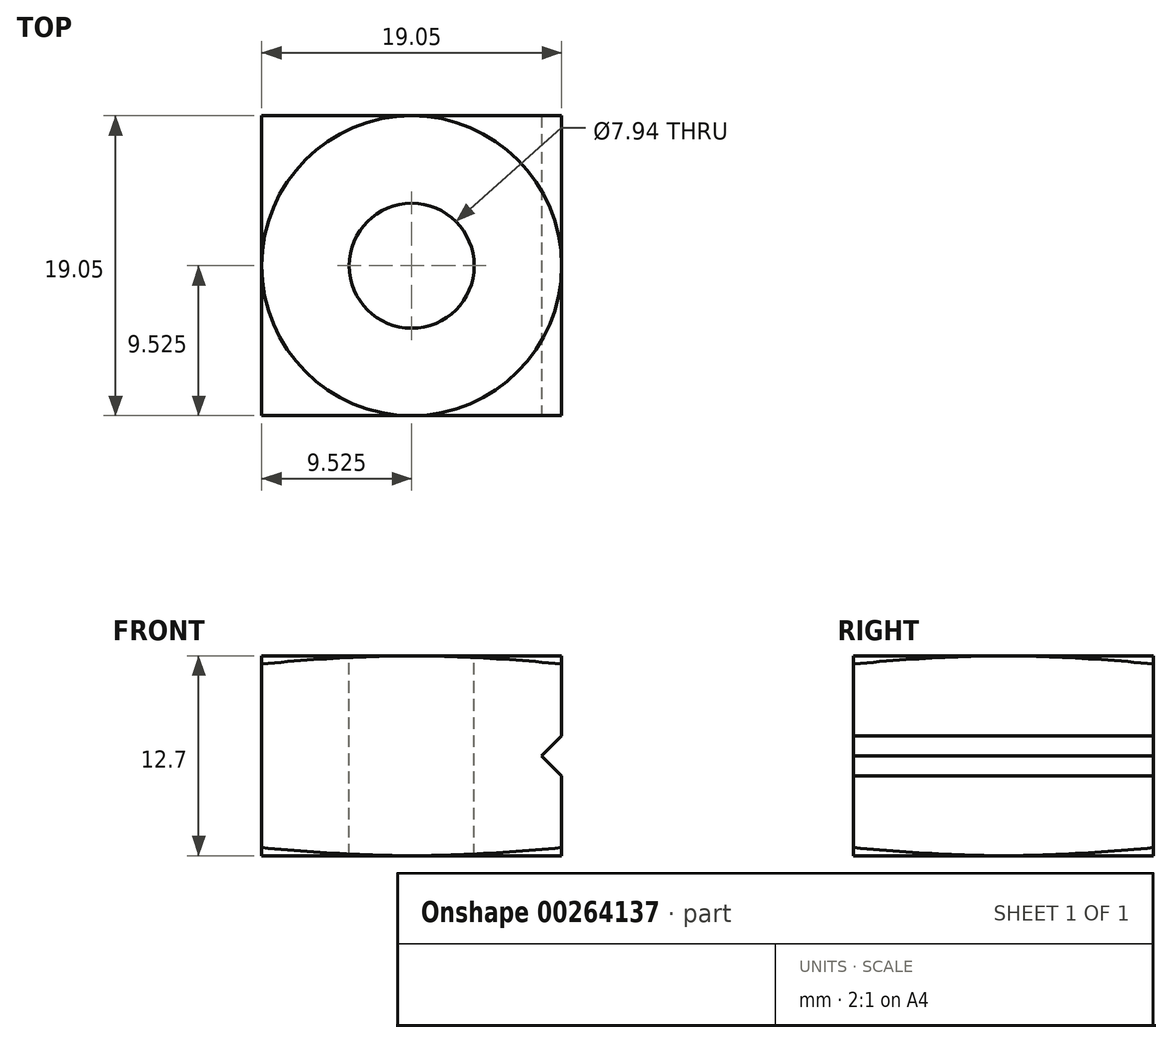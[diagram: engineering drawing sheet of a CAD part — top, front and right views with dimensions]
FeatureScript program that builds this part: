
annotation { "Feature Type Name" : "Feature", "Feature Type Description" : "" }
export const myFeature = defineFeature(function(context is Context, id is Id, definition is map)
    precondition{}
    {
        {
            var Q0;
            Q0=qCreatedBy(makeId("Top.planeOp"),FACE);
            var sketch = newSketch(context, id + "F0", { "sketchPlane" : qUnion([Q0])});
            skLineSegment(sketch, "E0.bottom", {"start": v(0, 0) * mm, "end": v(-19.05, 0) * mm});
            skLineSegment(sketch, "E0.top", {"start": v(0, 19.05) * mm, "end": v(-19.05, 19.05) * mm});
            skLineSegment(sketch, "E0.left", {"start": v(0, 0) * mm, "end": v(0, 19.05) * mm});
            skLineSegment(sketch, "E0.right", {"start": v(-19.05, 0) * mm, "end": v(-19.05, 19.05) * mm});
            skSolve(sketch);
        }
        {
            var Q0;
            Q0=makeQuery(id+"F0.imprint","IMPRINT",FACE,{"disambiguationData":[TD([[makeQuery(id+"F0.imprint","IMPRINT",EDGE,{"derivedFrom":sQuery(id+"F0.wireOp",EDGE,"E0.bottom")}),-1.0]])]});
            extrude(context, id + "F1", {"entities" : qUnion([Q0]), "depth" : 12.7 * mm});
        }
        {
            var Q0;
            Q0=makeQuery(id+"F1.opExtrude","CAP_FACE",FACE,{"disambiguationData":[OSD([sQuery(id+"F0.wireOp",EDGE,"E0.bottom"),sQuery(id+"F0.wireOp",EDGE,"E0.top"),sQuery(id+"F0.wireOp",EDGE,"E0.left"),sQuery(id+"F0.wireOp",EDGE,"E0.right")])],"isStart":false});
            var sketch = newSketch(context, id + "F2", { "sketchPlane" : qUnion([Q0])});
            skCircle(sketch, "E1", {"center": v(-9.53, 9.53) * mm, "radius": 3.97 * mm});
            skSolve(sketch);
        }
        {
            var Q0;
            Q0 = qSketchRegion(id + "F2", true);
            extrude(context, id + "F3", {"entities" : qUnion([Q0]), "operationType" : NewBodyOperationType.REMOVE, "endBound" : BoundingType.THROUGH_ALL, "oppositeDirection" : true, "depth" : 25.4 * mm});
        }
        {
            var Q0;
            Q0=makeQuery(id+"F2.imprint","IMPRINT",FACE,{"disambiguationData":[TD([[makeQuery(id+"F2.imprint","IMPRINT",EDGE,{"derivedFrom":sQuery(id+"F2.wireOp",EDGE,"E1")}),-1.0]])]});
            var sketch = newSketch(context, id + "F4", { "sketchPlane" : qUnion([Q0])});
            skCircle(sketch, "E2", {"center": v(-9.53, 9.53) * mm, "radius": 9.53 * mm});
            skSolve(sketch);
        }
        {
            var Q0;
            Q0=makeQuery(id+"F1.opExtrude","SWEPT_FACE",FACE,{"disambiguationData":[OSD([sQuery(id+"F0.wireOp",EDGE,"E0.bottom")])]});
            var Q1;
            Q1=makeQuery(id+"F1.opExtrude","SWEPT_FACE",FACE,{"disambiguationData":[OSD([sQuery(id+"F0.wireOp",EDGE,"E0.top")])]});
            cPlane(context, id + "F5", {"entities" : qUnion([Q0, Q1]), "cplaneType" : CPlaneType.MID_PLANE, "offset" : 25.4 * mm, "width" : 152.4 * mm, "height" : 152.4 * mm});
        }
        {
            var Q0;
            Q0=qCreatedBy(id+"F5.planeOp",FACE);
            var sketch = newSketch(context, id + "F6", { "sketchPlane" : qUnion([Q0])});
            skLineSegment(sketch, "E3.0.0", {"start": v(0, 0) * mm, "end": v(-19.05, 0) * mm});
            skLineSegment(sketch, "E3.0.1", {"start": v(-19.05, 0) * mm, "end": v(-19.05, 12.7) * mm});
            skLineSegment(sketch, "E3.0.2", {"start": v(-19.05, 12.7) * mm, "end": v(0, 12.7) * mm});
            skLineSegment(sketch, "E3.0.3", {"start": v(0, 12.7) * mm, "end": v(0, 0) * mm});
            skLineSegment(sketch, "E4", {"start": v(-19.05, 12.7) * mm, "end": v(-24.62, 11.97) * mm});
            skLineSegment(sketch, "E5", {"start": v(-24.62, 11.97) * mm, "end": v(-24.62, 13.43) * mm});
            skLineSegment(sketch, "E6", {"start": v(-24.62, 13.43) * mm, "end": v(-19.05, 12.7) * mm});
            skLineSegment(sketch, "E7", {"start": v(-19.05, 12.7) * mm, "end": v(-24.62, 12.7) * mm, "construction": true});
            skSolve(sketch);
        }
        {
            var Q0;
            Q0=makeQuery(id+"F6.imprint","IMPRINT",FACE,{"disambiguationData":[TD([[makeQuery(id+"F6.imprint","IMPRINT",EDGE,{"derivedFrom":sQuery(id+"F6.wireOp",EDGE,"E4")}),-1.0]])]});
            var Q1;
            Q1=sQuery(id+"F4.wireOp",EDGE,"E2");
            sweep(context, id + "F7", {"operationType" : NewBodyOperationType.REMOVE, "profiles" : qUnion([Q0]), "path" : qUnion([Q1])});
        }
        {
            var Q0;
            Q0=makeQuery(id+"F1.opExtrude","SWEPT_FACE",FACE,{"disambiguationData":[OSD([sQuery(id+"F0.wireOp",EDGE,"E0.bottom")])]});
            var Q1;
            Q1=makeQuery(id+"F1.opExtrude","SWEPT_FACE",FACE,{"disambiguationData":[OSD([sQuery(id+"F0.wireOp",EDGE,"E0.top")])]});
            cPlane(context, id + "F8", {"entities" : qUnion([Q0, Q1]), "cplaneType" : CPlaneType.MID_PLANE, "offset" : 25.4 * mm, "width" : 152.4 * mm, "height" : 152.4 * mm});
        }
        {
            var Q0;
            Q0=qCreatedBy(id+"F8.planeOp",FACE);
            var sketch = newSketch(context, id + "F9", { "sketchPlane" : qUnion([Q0])});
            skLineSegment(sketch, "E8", {"start": v(0, 0) * mm, "end": v(8.29, 1.1) * mm});
            skLineSegment(sketch, "E9", {"start": v(0, 0) * mm, "end": v(8.29, -1.1) * mm});
            skLineSegment(sketch, "E10", {"start": v(8.29, -1.1) * mm, "end": v(8.29, 1.1) * mm});
            skLineSegment(sketch, "E11", {"start": v(8.29, 0) * mm, "end": v(0, 0) * mm});
            skLineSegment(sketch, "E12", {"start": v(0, 0) * mm, "end": v(16.11, 0) * mm, "construction": true});
            skSolve(sketch);
        }
        {
            var Q0;
            {var subQ0=sQuery(id+"F9.wireOp",EDGE,"E9");Q0=makeQuery(id+"F9.imprint","IMPRINT",FACE,{"disambiguationData":[TD([[makeQuery(id+"F9.imprint","IMPRINT",EDGE,{"derivedFrom":subQ0}),1.0]])]});}
            var Q1;
            {var subQ0=sQuery(id+"F9.wireOp",EDGE,"E8");Q1=makeQuery(id+"F9.imprint","IMPRINT",FACE,{"disambiguationData":[TD([[makeQuery(id+"F9.imprint","IMPRINT",EDGE,{"derivedFrom":subQ0}),-1.0]])]});}
            var Q2;
            Q2=makeQuery(id+"F3.boolean.opBoolean","COPY",FACE,{"derivedFrom":makeQuery(id+"F3.opExtrude","SWEPT_FACE",FACE,{"disambiguationData":[OSD([sQuery(id+"F2.wireOp",EDGE,"E1")])]})});
            revolve(context, id + "F10", {"operationType" : NewBodyOperationType.REMOVE, "entities" : qUnion([Q0, Q1]), "axis" : qUnion([Q2]), "revolveType" : RevolveType.FULL, "oppositeDirection" : true});
        }
        {
            var Q0;
            Q0=makeQuery(id+"F1.opExtrude","SWEPT_FACE",FACE,{"disambiguationData":[OSD([sQuery(id+"F0.wireOp",EDGE,"E0.bottom")])]});
            var sketch = newSketch(context, id + "F11", { "sketchPlane" : qUnion([Q0])});
            skLineSegment(sketch, "E13", {"start": v(-1.27, 6.35) * mm, "end": v(0, 5.08) * mm});
            skPoint(sketch, "E13.startSnap0", {"position": v(0, 6.35) * mm});
            skLineSegment(sketch, "E14", {"start": v(-1.27, 6.35) * mm, "end": v(0, 7.62) * mm});
            skLineSegment(sketch, "E15", {"start": v(0, 7.62) * mm, "end": v(0, 5.08) * mm});
            skLineSegment(sketch, "E16", {"start": v(-1.27, 6.35) * mm, "end": v(0, 6.35) * mm, "construction": true});
            skSolve(sketch);
        }
        {
            var Q0;
            Q0 = qSketchRegion(id + "F11", true);
            extrude(context, id + "F12", {"entities" : qUnion([Q0]), "operationType" : NewBodyOperationType.REMOVE, "oppositeDirection" : true, "depth" : 19.05 * mm});
        }
    });
